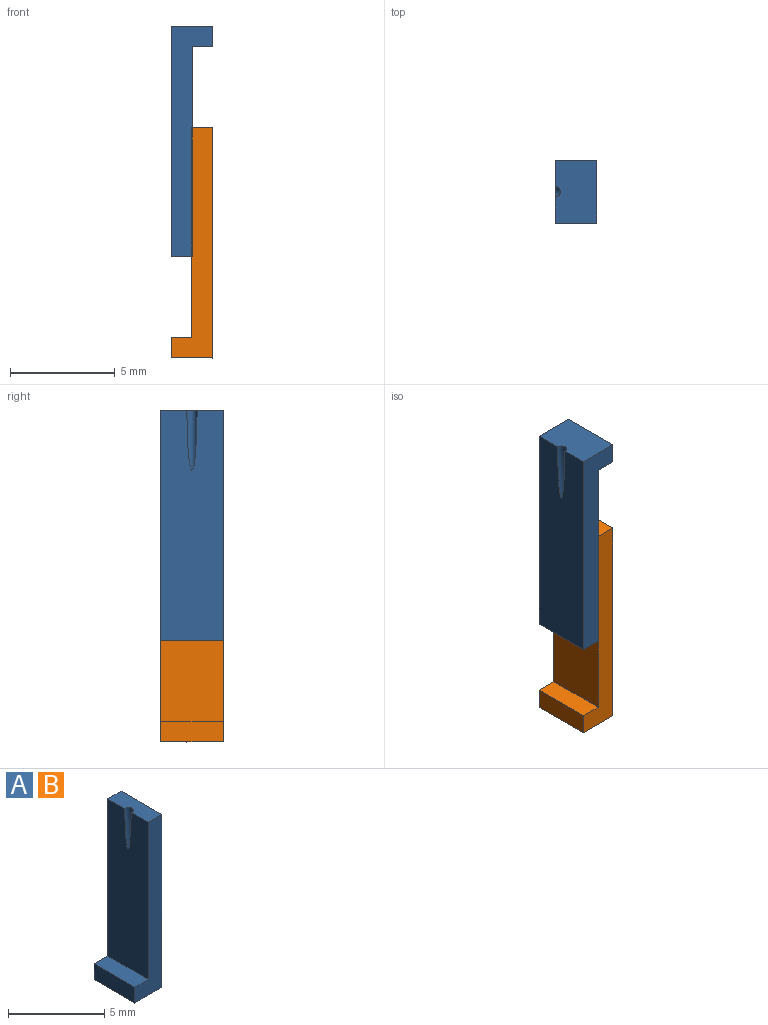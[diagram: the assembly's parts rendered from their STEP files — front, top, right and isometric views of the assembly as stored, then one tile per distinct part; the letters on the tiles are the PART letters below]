
ASSEMBLY  parts=2 mates=2
PART A: 9 faces, bbox 2.2x3x11 mm
  f0: plane 3x2mm, normal (0,0,-1), area 5.9mm2, adj f1,f3,f4,f5,f8
  f1: plane 11x3mm, normal (1,0,0), area 31.9mm2, adj f0,f4,f5,f7,f8
  f2: plane 3x1mm, normal (0,0,1), area 3mm2, adj f3,f4,f5,f6
  f3: plane 3x1mm, normal (-1,0,0), area 3mm2, adj f0,f2,f4,f5
  f4: plane 11x2mm, normal (0,-1,0), area 12mm2, adj f0,f1,f2,f3,f6,f7
  f5: plane 11x2mm, normal (0,1,0), area 12mm2, adj f0,f1,f2,f3,f6,f7
  f6: plane 10x3mm, normal (-1,0,0), area 29.1mm2, adj f2,f4,f5,f7,f8
  f7: plane 3x1mm, normal (0,0,1), area 2.9mm2, adj f1,f4,f5,f6,f8
  f8: cylinder r=0.25mm len=11.05mm, axis (0.09,0,-1), area 14.8mm2, adj f0,f1,f6,f7
PART B: same geometry as A
PLACE A rot(axis=(0,1,0),180deg) t=(2,3,14.87)mm
PLACE B t=(0,3,-1)mm
MATE planar A.f6 <-> B.f6  axis (1,0,0) through (1,0,8.87)mm
MATE planar A.f4 <-> B.f4  axis (0,-1,0) through (0.58,0,9.79)mm
